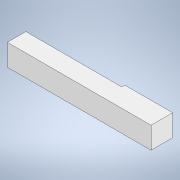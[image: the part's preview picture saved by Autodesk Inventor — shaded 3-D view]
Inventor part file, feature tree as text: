
AUTODESK INVENTOR PART (.ipt)
format: ipt  version: 2021 (Build 250183000, 183)  size: 96,768 bytes
history: native  units: in
note: dims shown in document units (in); Inventor stores cm internally (conversion verified against a paired STEP export)
features: extrude x1, sketch x1
ambient origin geometry x8: Origin, YZ Plane, XZ Plane, XY Plane, X Axis, Y Axis, Z Axis, Center Point
bodies: Solid1 (feature_tree)
feature tree (2):
  extrude  "Extrusion1"  Depth=3.875in
  sketch  "Sketch1"  dims[d0=0.875in d2=3.875in d6=0.875in d7=0.0in d8=0.75in d9=5.8125in]
